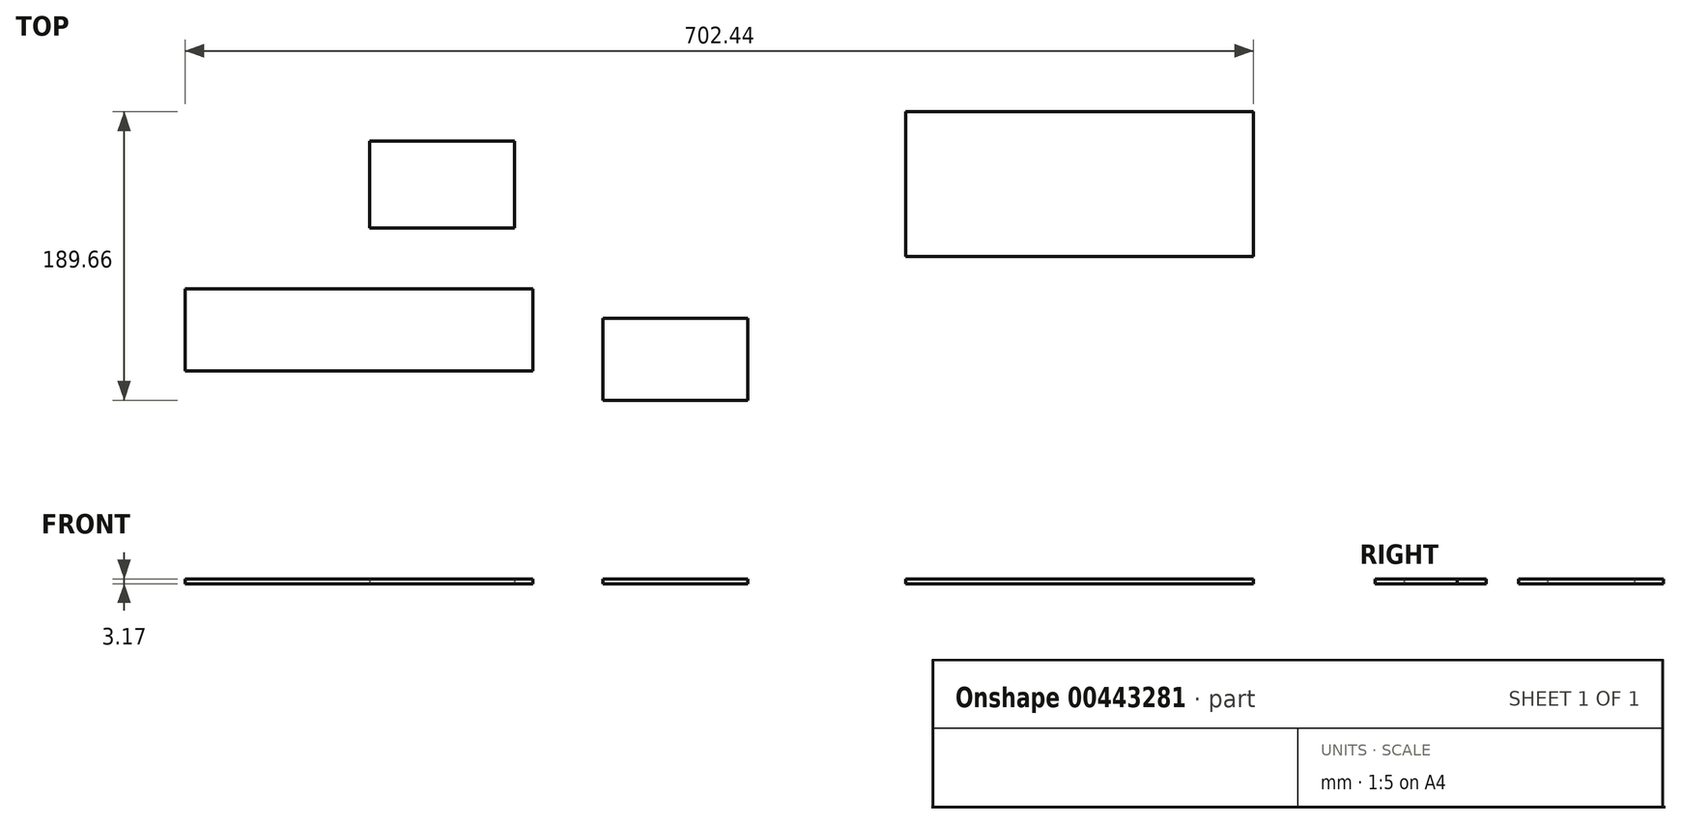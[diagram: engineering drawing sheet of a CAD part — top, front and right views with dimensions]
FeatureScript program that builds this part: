
annotation { "Feature Type Name" : "Feature", "Feature Type Description" : "" }
export const myFeature = defineFeature(function(context is Context, id is Id, definition is map)
    precondition{}
    {
        {
            var Q0;
            Q0=qCreatedBy(makeId("Top.planeOp"),FACE);
            var sketch = newSketch(context, id + "F0", { "sketchPlane" : qUnion([Q0])});
            skLineSegment(sketch, "E0", {"start": v(0, 0) * mm, "end": v(0, 95.25) * mm});
            skLineSegment(sketch, "E1", {"start": v(0, 95.25) * mm, "end": v(-228.6, 95.25) * mm});
            skLineSegment(sketch, "E2", {"start": v(-228.6, 95.25) * mm, "end": v(-228.6, 0) * mm});
            skLineSegment(sketch, "E3", {"start": v(-228.6, 0) * mm, "end": v(0, 0) * mm});
            skSolve(sketch);
        }
        {
            var Q0;
            Q0=makeQuery(id+"F0.imprint","IMPRINT",FACE,{"disambiguationData":[TD([[makeQuery(id+"F0.imprint","IMPRINT",EDGE,{"derivedFrom":sQuery(id+"F0.wireOp",EDGE,"E0")}),1.0]])]});
            extrude(context, id + "F1", {"entities" : qUnion([Q0]), "depth" : 3.17 * mm});
        }
        {
            var Q0;
            Q0=qCreatedBy(makeId("Top.planeOp"),FACE);
            var sketch = newSketch(context, id + "F2", { "sketchPlane" : qUnion([Q0])});
            skLineSegment(sketch, "E4.bottom", {"start": v(-581.06, 75.97) * mm, "end": v(-485.81, 75.97) * mm});
            skLineSegment(sketch, "E4.top", {"start": v(-581.06, 18.82) * mm, "end": v(-485.81, 18.82) * mm});
            skLineSegment(sketch, "E4.left", {"start": v(-581.06, 75.97) * mm, "end": v(-581.06, 18.82) * mm});
            skLineSegment(sketch, "E4.right", {"start": v(-485.81, 75.97) * mm, "end": v(-485.81, 18.82) * mm});
            skSolve(sketch);
        }
        {
            var Q0;
            Q0=makeQuery(id+"F2.imprint","IMPRINT",FACE,{"disambiguationData":[TD([[makeQuery(id+"F2.imprint","IMPRINT",EDGE,{"derivedFrom":sQuery(id+"F2.wireOp",EDGE,"E4.bottom")}),-1.0]])]});
            extrude(context, id + "F3", {"entities" : qUnion([Q0]), "depth" : 3.17 * mm});
        }
        {
            var Q0;
            Q0=qCreatedBy(makeId("Top.planeOp"),FACE);
            var sketch = newSketch(context, id + "F4", { "sketchPlane" : qUnion([Q0])});
            skLineSegment(sketch, "E5.bottom", {"start": v(-427.77, -40.43) * mm, "end": v(-332.52, -40.43) * mm});
            skLineSegment(sketch, "E5.top", {"start": v(-427.77, -94.4) * mm, "end": v(-332.52, -94.4) * mm});
            skLineSegment(sketch, "E5.left", {"start": v(-427.77, -40.43) * mm, "end": v(-427.77, -94.4) * mm});
            skLineSegment(sketch, "E5.right", {"start": v(-332.52, -40.43) * mm, "end": v(-332.52, -94.4) * mm});
            skSolve(sketch);
        }
        {
            var Q0;
            Q0=makeQuery(id+"F4.imprint","IMPRINT",FACE,{"disambiguationData":[TD([[makeQuery(id+"F4.imprint","IMPRINT",EDGE,{"derivedFrom":sQuery(id+"F4.wireOp",EDGE,"E5.bottom")}),-1.0]])]});
            extrude(context, id + "F5", {"entities" : qUnion([Q0]), "depth" : 3.17 * mm});
        }
        {
            var Q0;
            Q0=qCreatedBy(makeId("Top.planeOp"),FACE);
            var sketch = newSketch(context, id + "F6", { "sketchPlane" : qUnion([Q0])});
            skLineSegment(sketch, "E6.bottom", {"start": v(-702.44, -21.26) * mm, "end": v(-473.84, -21.26) * mm});
            skLineSegment(sketch, "E6.top", {"start": v(-702.44, -75.23) * mm, "end": v(-473.84, -75.23) * mm});
            skLineSegment(sketch, "E6.left", {"start": v(-702.44, -21.26) * mm, "end": v(-702.44, -75.23) * mm});
            skLineSegment(sketch, "E6.right", {"start": v(-473.84, -21.26) * mm, "end": v(-473.84, -75.23) * mm});
            skSolve(sketch);
        }
        {
            var Q0;
            Q0=makeQuery(id+"F6.imprint","IMPRINT",FACE,{"disambiguationData":[TD([[makeQuery(id+"F6.imprint","IMPRINT",EDGE,{"derivedFrom":sQuery(id+"F6.wireOp",EDGE,"E6.bottom")}),-1.0]])]});
            extrude(context, id + "F7", {"entities" : qUnion([Q0]), "depth" : 3.17 * mm});
        }
    });
